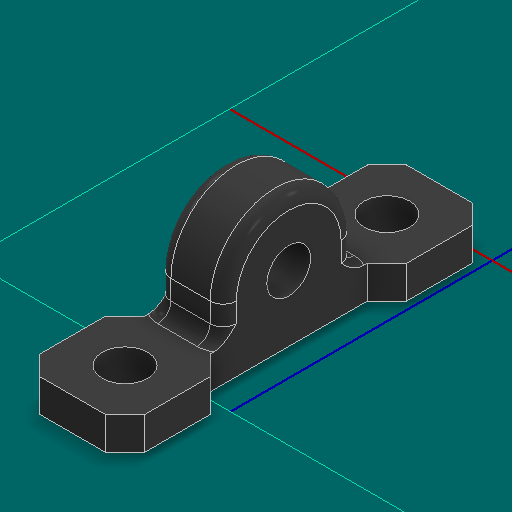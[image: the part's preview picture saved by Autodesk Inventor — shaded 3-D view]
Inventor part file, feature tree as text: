
AUTODESK INVENTOR PART (.ipt)
format: ipt  version: 2025 (Build 290162000, 162)  size: 206,848 bytes
history: native  units: in
note: dims shown in document units (in); Inventor stores cm internally (conversion verified against a paired STEP export)
features: other x3, sketch x3
ambient origin geometry x8: Origin, YZ Plane, XZ Plane, XY Plane, X Axis, Y Axis, Z Axis, Center Point
bodies: Solid1 (feature_tree)
feature tree (6):
  other  "LS Pillow Bearing Block.ipt"
  other  "Solid1::LS Pillow Bearing Block.ipt"
  other  "TaggingFeature1"
  sketch  "Sketch1"  dims[d0=0.3937in]
  sketch  "Sketch2"
  sketch  "Sketch3"
